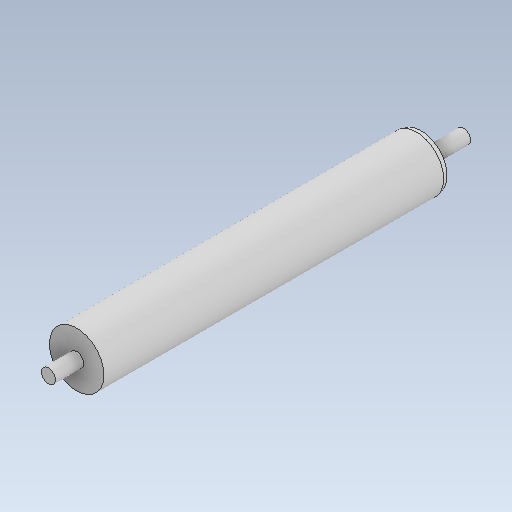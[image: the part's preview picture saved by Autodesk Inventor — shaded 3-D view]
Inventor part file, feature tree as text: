
AUTODESK INVENTOR PART (.ipt)
format: ipt  version: 2021 (Build 250183000, 183)  size: 118,784 bytes
history: native  units: mm
features: extrude x4, sketch x4, fillet x1
ambient origin geometry x8: Origin, YZ Plane, XZ Plane, XY Plane, X Axis, Y Axis, Z Axis, Center Point
bodies: Solid1 (feature_tree)
feature tree (9):
  extrude  "Extrusion1"  Depth=80.0mm TaperAngle=0.0deg
  fillet  "Fillet1"  Radius=2.0mm
  extrude  "Extrusion2"  Depth=11.56mm
  extrude  "Extrusion3"  Depth=1.0mm TaperAngle=0.0deg
  extrude  "Extrusion4"  [1 undecoded]
  sketch  "Sketch1"  dims[d0=11.56mm d1=80.0mm d2=0.0mm d3=2.0mm]
  sketch  "Sketch2"  dims[d4=3.0mm d5=11.56mm]
  sketch  "Sketch3"  dims[d6=6.0mm d7=0.0mm d8=1.0mm d9=0.0mm]
  sketch  "Sketch4"  dims[d10=8.0mm d11=0.0mm]
note: 1 required parameter value undecoded (feature->parameter linkage not recoverable at this tier; creation-order binding heuristic only, values carry confidence <= 0.55)
